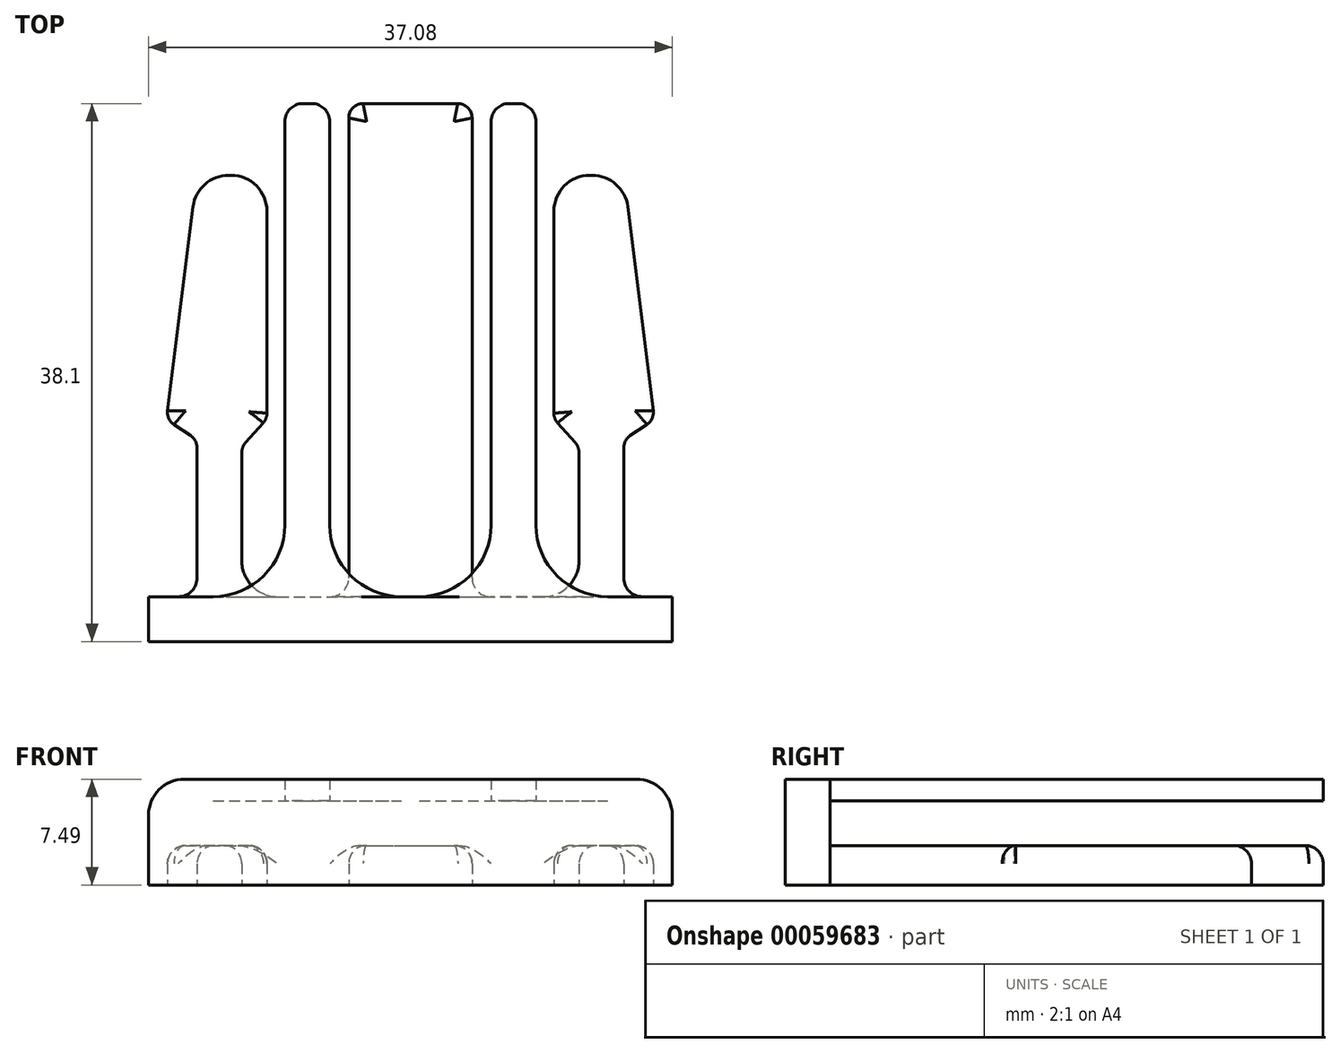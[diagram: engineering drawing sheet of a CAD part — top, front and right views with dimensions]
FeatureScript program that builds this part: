
annotation { "Feature Type Name" : "Feature", "Feature Type Description" : "" }
export const myFeature = defineFeature(function(context is Context, id is Id, definition is map)
    precondition{}
    {
        {
            var Q0;
            Q0=qCreatedBy(makeId("Top.planeOp"),FACE);
            var sketch = newSketch(context, id + "F0", { "sketchPlane" : qUnion([Q0])});
            skLineSegment(sketch, "E0", {"start": v(0, -24.5) * mm, "end": v(-18.54, -24.5) * mm});
            skLineSegment(sketch, "E1", {"start": v(-18.54, -24.5) * mm, "end": v(-18.54, -21.32) * mm});
            skLineSegment(sketch, "E2", {"start": v(-18.54, -21.32) * mm, "end": v(-15.11, -21.32) * mm});
            skLineSegment(sketch, "E3", {"start": v(-15.11, -21.32) * mm, "end": v(-15.11, -10.2) * mm});
            skLineSegment(sketch, "E4", {"start": v(-15.11, 8.53) * mm, "end": v(-11.94, 8.53) * mm});
            skLineSegment(sketch, "E5", {"start": v(-11.94, -10.7) * mm, "end": v(-11.94, -21.32) * mm});
            skLineSegment(sketch, "E6", {"start": v(-4.37, -21.32) * mm, "end": v(-4.37, 13.6) * mm});
            skLineSegment(sketch, "E7", {"start": v(-4.37, 13.6) * mm, "end": v(0, 13.6) * mm});
            skLineSegment(sketch, "E8", {"start": v(-15.11, -10.2) * mm, "end": v(-17.27, -8.78) * mm});
            skLineSegment(sketch, "E9", {"start": v(-17.27, -8.78) * mm, "end": v(-15.11, 8.53) * mm});
            skLineSegment(sketch, "E10", {"start": v(-11.94, 8.53) * mm, "end": v(-10.16, 8.53) * mm});
            skLineSegment(sketch, "E11", {"start": v(-10.16, 8.53) * mm, "end": v(-10.16, -8.7) * mm});
            skLineSegment(sketch, "E12", {"start": v(-10.16, -8.7) * mm, "end": v(-11.94, -10.7) * mm});
            skLineSegment(sketch, "E13.trimOffspring", {"start": v(-11.94, -21.32) * mm, "end": v(-4.37, -21.32) * mm});
            skLineSegment(sketch, "E14", {"start": v(0, 13.6) * mm, "end": v(0, 0) * mm});
            skLineSegment(sketch, "E15.MirrorCS", {"start": v(4.37, 13.6) * mm, "end": v(0, 13.6) * mm});
            skLineSegment(sketch, "E16.MirrorCS", {"start": v(4.37, -21.32) * mm, "end": v(4.37, 13.6) * mm});
            skLineSegment(sketch, "E17.MirrorCS", {"start": v(11.94, -21.32) * mm, "end": v(4.37, -21.32) * mm});
            skLineSegment(sketch, "E18.MirrorCS", {"start": v(11.94, -10.7) * mm, "end": v(11.94, -21.32) * mm});
            skLineSegment(sketch, "E19.MirrorCS", {"start": v(10.16, -8.7) * mm, "end": v(11.94, -10.7) * mm});
            skLineSegment(sketch, "E20.MirrorCS", {"start": v(10.16, 8.53) * mm, "end": v(10.16, -8.7) * mm});
            skLineSegment(sketch, "E21.MirrorCS", {"start": v(11.94, 8.53) * mm, "end": v(10.16, 8.53) * mm});
            skLineSegment(sketch, "E22.MirrorCS", {"start": v(15.11, 8.53) * mm, "end": v(11.94, 8.53) * mm});
            skLineSegment(sketch, "E23.MirrorCS", {"start": v(17.27, -8.78) * mm, "end": v(15.11, 8.53) * mm});
            skLineSegment(sketch, "E24.MirrorCS", {"start": v(15.11, -10.2) * mm, "end": v(17.27, -8.78) * mm});
            skLineSegment(sketch, "E25.MirrorCS", {"start": v(15.11, -21.32) * mm, "end": v(15.11, -10.2) * mm});
            skLineSegment(sketch, "E26.MirrorCS", {"start": v(18.54, -21.32) * mm, "end": v(15.11, -21.32) * mm});
            skLineSegment(sketch, "E27.MirrorCS", {"start": v(18.54, -24.5) * mm, "end": v(18.54, -21.32) * mm});
            skLineSegment(sketch, "E28.MirrorCS", {"start": v(0, -24.5) * mm, "end": v(18.54, -24.5) * mm});
            skSolve(sketch);
        }
        {
            var Q0;
            Q0=makeQuery(id+"F0.imprint","IMPRINT",FACE,{"disambiguationData":[TD([[makeQuery(id+"F0.imprint","IMPRINT",EDGE,{"derivedFrom":sQuery(id+"F0.wireOp",EDGE,"E0")}),-1.0]])]});
            extrude(context, id + "F1", {"entities" : qUnion([Q0]), "depth" : 2.8 * mm});
        }
        {
            var Q0;
            Q0=makeQuery(id+"F1.opExtrude","SWEPT_EDGE",EDGE,{"disambiguationData":[OSD([sQuery(id+"F0.wireOp",EDGE,"E8"),sQuery(id+"F0.wireOp",EDGE,"E9")])]});
            var Q1;
            Q1=makeQuery(id+"F1.opExtrude","SWEPT_EDGE",EDGE,{"disambiguationData":[OSD([sQuery(id+"F0.wireOp",EDGE,"E5"),sQuery(id+"F0.wireOp",EDGE,"E12")])]});
            var Q2;
            Q2=makeQuery(id+"F1.opExtrude","SWEPT_EDGE",EDGE,{"disambiguationData":[OSD([sQuery(id+"F0.wireOp",EDGE,"E11"),sQuery(id+"F0.wireOp",EDGE,"E12")])]});
            var Q3;
            Q3=makeQuery(id+"F1.opExtrude","SWEPT_EDGE",EDGE,{"disambiguationData":[OSD([sQuery(id+"F0.wireOp",EDGE,"5dbca827-9765-4d0b-b738-52eea5b91d420.MirrorCS"),sQuery(id+"F0.wireOp",EDGE,"41e8d5a4-3eae-4dab-9418-c4afa11fb4a70.MirrorCS")])]});
            var Q4;
            Q4=makeQuery(id+"F1.opExtrude","SWEPT_EDGE",EDGE,{"disambiguationData":[OSD([sQuery(id+"F0.wireOp",EDGE,"c12c2d76-7289-4d38-adec-d10e20b737c40.MirrorCS"),sQuery(id+"F0.wireOp",EDGE,"84a0010f-25cf-47dd-b195-3eac934034af0.MirrorCS")])]});
            var Q5;
            Q5=makeQuery(id+"F1.opExtrude","SWEPT_EDGE",EDGE,{"disambiguationData":[OSD([sQuery(id+"F0.wireOp",EDGE,"67a6e3c0-60ff-418f-9d16-aaa68642b8130.MirrorCS"),sQuery(id+"F0.wireOp",EDGE,"c12c2d76-7289-4d38-adec-d10e20b737c40.MirrorCS")])]});
            var Q6;
            Q6=makeQuery(id+"F1.opExtrude","SWEPT_EDGE",EDGE,{"disambiguationData":[OSD([sQuery(id+"F0.wireOp",EDGE,"E3"),sQuery(id+"F0.wireOp",EDGE,"E8")])]});
            var Q7;
            Q7=makeQuery(id+"F1.opExtrude","SWEPT_EDGE",EDGE,{"disambiguationData":[OSD([sQuery(id+"F0.wireOp",EDGE,"182dc025-4c15-4511-8ecc-ef8c38a5272f0.MirrorCS"),sQuery(id+"F0.wireOp",EDGE,"41e8d5a4-3eae-4dab-9418-c4afa11fb4a70.MirrorCS")])]});
            var Q8;
            Q8=makeQuery(id+"F1.opExtrude","SWEPT_EDGE",EDGE,{"disambiguationData":[OSD([sQuery(id+"F0.wireOp",EDGE,"f6ebb351-b71a-4f62-886c-60468f4f10860.MirrorCS"),sQuery(id+"F0.wireOp",EDGE,"eb93e29c-52ff-4c8f-8371-2f97ac019cd80.MirrorCS")])]});
            var Q9;
            Q9=makeQuery(id+"F1.opExtrude","SWEPT_EDGE",EDGE,{"disambiguationData":[OSD([sQuery(id+"F0.wireOp",EDGE,"E6"),sQuery(id+"F0.wireOp",EDGE,"E7")])]});
            var Q10;
            Q10=makeQuery(id+"F1.opExtrude","SWEPT_EDGE",EDGE,{"disambiguationData":[OSD([sQuery(id+"F0.wireOp",EDGE,"E15.MirrorCS"),sQuery(id+"F0.wireOp",EDGE,"E16.MirrorCS")])]});
            var Q11;
            Q11=makeQuery(id+"F1.opExtrude","SWEPT_EDGE",EDGE,{"disambiguationData":[OSD([sQuery(id+"F0.wireOp",EDGE,"E23.MirrorCS"),sQuery(id+"F0.wireOp",EDGE,"E24.MirrorCS")])]});
            var Q12;
            Q12=makeQuery(id+"F1.opExtrude","SWEPT_EDGE",EDGE,{"disambiguationData":[OSD([sQuery(id+"F0.wireOp",EDGE,"E24.MirrorCS"),sQuery(id+"F0.wireOp",EDGE,"E25.MirrorCS")])]});
            var Q13;
            Q13=makeQuery(id+"F1.opExtrude","SWEPT_EDGE",EDGE,{"disambiguationData":[OSD([sQuery(id+"F0.wireOp",EDGE,"E18.MirrorCS"),sQuery(id+"F0.wireOp",EDGE,"E19.MirrorCS")])]});
            var Q14;
            Q14=makeQuery(id+"F1.opExtrude","SWEPT_EDGE",EDGE,{"disambiguationData":[OSD([sQuery(id+"F0.wireOp",EDGE,"E19.MirrorCS"),sQuery(id+"F0.wireOp",EDGE,"E20.MirrorCS")])]});
            fillet(context, id + "F2", {"entities" : qUnion([Q0, Q1, Q2, Q3, Q4, Q5, Q6, Q7, Q8, Q9, Q10, Q11, Q12, Q13, Q14]), "radius" : 1.02 * mm, "tangentPropagation" : true, "allowEdgeOverflow" : false});
        }
        {
            var Q0;
            Q0=makeQuery(id+"F1.opExtrude","SWEPT_EDGE",EDGE,{"disambiguationData":[OSD([sQuery(id+"F0.wireOp",EDGE,"E2"),sQuery(id+"F0.wireOp",EDGE,"E3")])]});
            var Q1;
            Q1=makeQuery(id+"F1.opExtrude","SWEPT_EDGE",EDGE,{"disambiguationData":[OSD([sQuery(id+"F0.wireOp",EDGE,"043e1b75-f5ca-422c-ab0a-28e3224b58670.MirrorCS"),sQuery(id+"F0.wireOp",EDGE,"182dc025-4c15-4511-8ecc-ef8c38a5272f0.MirrorCS")])]});
            var Q2;
            Q2=makeQuery(id+"F1.opExtrude","SWEPT_EDGE",EDGE,{"disambiguationData":[OSD([sQuery(id+"F0.wireOp",EDGE,"eb93e29c-52ff-4c8f-8371-2f97ac019cd80.MirrorCS"),sQuery(id+"F0.wireOp",EDGE,"24293765-a530-4c86-9293-c4c4a651b3b3.trimOffspring")])]});
            var Q3;
            Q3=makeQuery(id+"F1.opExtrude","SWEPT_EDGE",EDGE,{"disambiguationData":[OSD([sQuery(id+"F0.wireOp",EDGE,"E6"),sQuery(id+"F0.wireOp",EDGE,"E13.trimOffspring")])]});
            var Q4;
            Q4=makeQuery(id+"F1.opExtrude","SWEPT_EDGE",EDGE,{"disambiguationData":[OSD([sQuery(id+"F0.wireOp",EDGE,"E16.MirrorCS"),sQuery(id+"F0.wireOp",EDGE,"E17.MirrorCS")])]});
            var Q5;
            Q5=makeQuery(id+"F1.opExtrude","SWEPT_EDGE",EDGE,{"disambiguationData":[OSD([sQuery(id+"F0.wireOp",EDGE,"E25.MirrorCS"),sQuery(id+"F0.wireOp",EDGE,"E26.MirrorCS")])]});
            fillet(context, id + "F3", {"entities" : qUnion([Q0, Q1, Q2, Q3, Q4, Q5]), "radius" : 1.32 * mm, "tangentPropagation" : true, "allowEdgeOverflow" : false});
        }
        {
            var Q0;
            Q0=makeQuery(id+"F1.opExtrude","SWEPT_EDGE",EDGE,{"disambiguationData":[OSD([sQuery(id+"F0.wireOp",EDGE,"67a6e3c0-60ff-418f-9d16-aaa68642b8130.MirrorCS"),sQuery(id+"F0.wireOp",EDGE,"24293765-a530-4c86-9293-c4c4a651b3b3.trimOffspring")])]});
            var Q1;
            Q1=makeQuery(id+"F1.opExtrude","SWEPT_EDGE",EDGE,{"disambiguationData":[OSD([sQuery(id+"F0.wireOp",EDGE,"E5"),sQuery(id+"F0.wireOp",EDGE,"E13.trimOffspring")])]});
            var Q2;
            Q2=makeQuery(id+"F1.opExtrude","SWEPT_EDGE",EDGE,{"disambiguationData":[OSD([sQuery(id+"F0.wireOp",EDGE,"44883f8e-5c6c-496e-87a4-7bb2ec8b31cd0.MirrorCS"),sQuery(id+"F0.wireOp",EDGE,"5dbca827-9765-4d0b-b738-52eea5b91d420.MirrorCS")])]});
            var Q3;
            Q3=makeQuery(id+"F1.opExtrude","SWEPT_EDGE",EDGE,{"disambiguationData":[OSD([sQuery(id+"F0.wireOp",EDGE,"84a0010f-25cf-47dd-b195-3eac934034af0.MirrorCS"),sQuery(id+"F0.wireOp",EDGE,"d00008af-d735-409f-bce0-33d418154a760.MirrorCS")])]});
            var Q4;
            Q4=makeQuery(id+"F1.opExtrude","SWEPT_EDGE",EDGE,{"disambiguationData":[OSD([sQuery(id+"F0.wireOp",EDGE,"E10"),sQuery(id+"F0.wireOp",EDGE,"E11")])]});
            var Q5;
            Q5=makeQuery(id+"F1.opExtrude","SWEPT_EDGE",EDGE,{"disambiguationData":[OSD([sQuery(id+"F0.wireOp",EDGE,"E4"),sQuery(id+"F0.wireOp",EDGE,"E9")])]});
            var Q6;
            Q6=makeQuery(id+"F1.opExtrude","SWEPT_EDGE",EDGE,{"disambiguationData":[OSD([sQuery(id+"F0.wireOp",EDGE,"E17.MirrorCS"),sQuery(id+"F0.wireOp",EDGE,"E18.MirrorCS")])]});
            var Q7;
            Q7=makeQuery(id+"F1.opExtrude","SWEPT_EDGE",EDGE,{"disambiguationData":[OSD([sQuery(id+"F0.wireOp",EDGE,"E20.MirrorCS"),sQuery(id+"F0.wireOp",EDGE,"E21.MirrorCS")])]});
            var Q8;
            Q8=makeQuery(id+"F1.opExtrude","SWEPT_EDGE",EDGE,{"disambiguationData":[OSD([sQuery(id+"F0.wireOp",EDGE,"E22.MirrorCS"),sQuery(id+"F0.wireOp",EDGE,"E23.MirrorCS")])]});
            fillet(context, id + "F4", {"entities" : qUnion([Q0, Q1, Q2, Q3, Q4, Q5, Q6, Q7, Q8]), "radius" : 2.54 * mm, "tangentPropagation" : true, "allowEdgeOverflow" : false});
        }
        {
            var Q0;
            Q0=makeQuery(id+"F1.opExtrude","CAP_FACE",FACE,{"disambiguationData":[OSD([sQuery(id+"F0.wireOp",EDGE,"E0"),sQuery(id+"F0.wireOp",EDGE,"E1"),sQuery(id+"F0.wireOp",EDGE,"E2"),sQuery(id+"F0.wireOp",EDGE,"E3"),sQuery(id+"F0.wireOp",EDGE,"E4"),sQuery(id+"F0.wireOp",EDGE,"E5"),sQuery(id+"F0.wireOp",EDGE,"E6"),sQuery(id+"F0.wireOp",EDGE,"E7"),sQuery(id+"F0.wireOp",EDGE,"E8"),sQuery(id+"F0.wireOp",EDGE,"E9"),sQuery(id+"F0.wireOp",EDGE,"E10"),sQuery(id+"F0.wireOp",EDGE,"E11"),sQuery(id+"F0.wireOp",EDGE,"E12"),sQuery(id+"F0.wireOp",EDGE,"E13.trimOffspring"),sQuery(id+"F0.wireOp",EDGE,"E15.MirrorCS"),sQuery(id+"F0.wireOp",EDGE,"E16.MirrorCS"),sQuery(id+"F0.wireOp",EDGE,"E17.MirrorCS"),sQuery(id+"F0.wireOp",EDGE,"E18.MirrorCS"),sQuery(id+"F0.wireOp",EDGE,"E19.MirrorCS"),sQuery(id+"F0.wireOp",EDGE,"E20.MirrorCS"),sQuery(id+"F0.wireOp",EDGE,"E21.MirrorCS"),sQuery(id+"F0.wireOp",EDGE,"E22.MirrorCS"),sQuery(id+"F0.wireOp",EDGE,"E23.MirrorCS"),sQuery(id+"F0.wireOp",EDGE,"E24.MirrorCS"),sQuery(id+"F0.wireOp",EDGE,"E25.MirrorCS"),sQuery(id+"F0.wireOp",EDGE,"E26.MirrorCS"),sQuery(id+"F0.wireOp",EDGE,"E27.MirrorCS"),sQuery(id+"F0.wireOp",EDGE,"E28.MirrorCS")])],"isStart":false});
            var sketch = newSketch(context, id + "F5", { "sketchPlane" : qUnion([Q0])});
            skLineSegment(sketch, "E29.bottom", {"start": v(-18.54, -24.5) * mm, "end": v(18.54, -24.5) * mm});
            skLineSegment(sketch, "E29.top", {"start": v(-18.54, -21.32) * mm, "end": v(18.54, -21.32) * mm});
            skLineSegment(sketch, "E29.left", {"start": v(-18.54, -24.5) * mm, "end": v(-18.54, -21.32) * mm});
            skLineSegment(sketch, "E29.right", {"start": v(18.54, -24.5) * mm, "end": v(18.54, -21.32) * mm});
            skSolve(sketch);
        }
        {
            var Q0;
            Q0 = qSketchRegion(id + "F5", true);
            extrude(context, id + "F6", {"entities" : qUnion([Q0]), "operationType" : NewBodyOperationType.ADD, "depth" : 3.17 * mm});
        }
        {
            var Q0;
            Q0=makeQuery(id+"F6.opExtrude","CAP_FACE",FACE,{"disambiguationData":[OSD([sQuery(id+"F5.wireOp",EDGE,"E29.bottom"),sQuery(id+"F5.wireOp",EDGE,"E29.top"),sQuery(id+"F5.wireOp",EDGE,"E29.left"),sQuery(id+"F5.wireOp",EDGE,"E29.right")])],"isStart":false});
            var sketch = newSketch(context, id + "F7", { "sketchPlane" : qUnion([Q0])});
            skLineSegment(sketch, "E30.bottom", {"start": v(-8.89, -24.5) * mm, "end": v(-5.71, -24.5) * mm});
            skLineSegment(sketch, "E30.top", {"start": v(-8.9, 13.6) * mm, "end": v(-5.72, 13.6) * mm});
            skLineSegment(sketch, "E30.left", {"start": v(-8.89, -21.32) * mm, "end": v(-8.9, 13.6) * mm});
            skLineSegment(sketch, "E30.right", {"start": v(-5.71, -21.32) * mm, "end": v(-5.72, 13.6) * mm});
            skLineSegment(sketch, "E31.MirrorCS", {"start": v(5.71, -21.32) * mm, "end": v(5.72, 13.6) * mm});
            skLineSegment(sketch, "E32.MirrorCS", {"start": v(8.9, 13.6) * mm, "end": v(5.72, 13.6) * mm});
            skLineSegment(sketch, "E33.MirrorCS", {"start": v(8.89, -21.32) * mm, "end": v(8.9, 13.6) * mm});
            skLineSegment(sketch, "E34.MirrorCS", {"start": v(8.89, -24.5) * mm, "end": v(5.71, -24.5) * mm});
            skLineSegment(sketch, "E35.bottom", {"start": v(-18.54, -24.5) * mm, "end": v(18.54, -24.5) * mm});
            skLineSegment(sketch, "E35.top", {"start": v(-18.54, -21.32) * mm, "end": v(-8.89, -21.32) * mm});
            skLineSegment(sketch, "E35.left", {"start": v(-18.54, -24.5) * mm, "end": v(-18.54, -21.32) * mm});
            skLineSegment(sketch, "E35.right", {"start": v(18.54, -24.5) * mm, "end": v(18.54, -21.32) * mm});
            skLineSegment(sketch, "E36.trimOffspring", {"start": v(-5.71, -21.32) * mm, "end": v(5.71, -21.32) * mm});
            skPoint(sketch, "E37.orphan", {"position": v(5.71, -24.5) * mm});
            skLineSegment(sketch, "E38.trimOffspring", {"start": v(8.89, -21.32) * mm, "end": v(18.54, -21.32) * mm});
            skPoint(sketch, "E39.orphan", {"position": v(8.89, -24.5) * mm});
            skSolve(sketch);
        }
        {
            var Q0;
            Q0 = qSketchRegion(id + "F7", true);
            extrude(context, id + "F8", {"entities" : qUnion([Q0]), "operationType" : NewBodyOperationType.ADD, "depth" : 1.52 * mm});
        }
        {
            var Q0;
            Q0=makeQuery(id+"F8.opExtrude","SWEPT_EDGE",EDGE,{"disambiguationData":[OSD([sQuery(id+"F5.wireOp",EDGE,"E29.top"),sQuery(id+"F7.wireOp",EDGE,"E33.MirrorCS"),sQuery(id+"F7.wireOp",EDGE,"E38.trimOffspring")])]});
            var Q1;
            Q1=makeQuery(id+"F8.opExtrude","SWEPT_EDGE",EDGE,{"disambiguationData":[OSD([sQuery(id+"F5.wireOp",EDGE,"E29.top"),sQuery(id+"F7.wireOp",EDGE,"E31.MirrorCS"),sQuery(id+"F7.wireOp",EDGE,"E36.trimOffspring")])]});
            var Q2;
            Q2=makeQuery(id+"F8.opExtrude","SWEPT_EDGE",EDGE,{"disambiguationData":[OSD([sQuery(id+"F5.wireOp",EDGE,"E29.top"),sQuery(id+"F7.wireOp",EDGE,"E30.right"),sQuery(id+"F7.wireOp",EDGE,"E36.trimOffspring")])]});
            var Q3;
            Q3=makeQuery(id+"F8.opExtrude","SWEPT_EDGE",EDGE,{"disambiguationData":[OSD([sQuery(id+"F5.wireOp",EDGE,"E29.top"),sQuery(id+"F7.wireOp",EDGE,"E30.left"),sQuery(id+"F7.wireOp",EDGE,"E35.top")])]});
            fillet(context, id + "F9", {"entities" : qUnion([Q0, Q1, Q2, Q3]), "radius" : 5.08 * mm, "tangentPropagation" : true, "allowEdgeOverflow" : false});
        }
        {
            var Q0;
            Q0=makeQuery(id+"F1.opExtrude","CAP_EDGE",EDGE,{"disambiguationData":[OSD([sQuery(id+"F0.wireOp",EDGE,"E9")])],"isStart":false});
            var Q1;
            {var subQ0=sQuery(id+"F0.wireOp",EDGE,"E9");var subQ1=sQuery(id+"F0.wireOp",EDGE,"E4");Q1=makeQuery(id+"F4.opFillet","BLEND_EDGE",EDGE,{"blendedFrom":[makeQuery(id+"F1.opExtrude","SWEPT_EDGE",EDGE,{"disambiguationData":[OSD([subQ1,subQ0])]}),makeQuery(id+"F1.opExtrude","CAP_FACE",FACE,{"disambiguationData":[OSD([sQuery(id+"F0.wireOp",EDGE,"E0"),sQuery(id+"F0.wireOp",EDGE,"E1"),sQuery(id+"F0.wireOp",EDGE,"E2"),sQuery(id+"F0.wireOp",EDGE,"E3"),subQ1,sQuery(id+"F0.wireOp",EDGE,"E5"),sQuery(id+"F0.wireOp",EDGE,"E6"),sQuery(id+"F0.wireOp",EDGE,"E7"),sQuery(id+"F0.wireOp",EDGE,"E8"),subQ0,sQuery(id+"F0.wireOp",EDGE,"E10"),sQuery(id+"F0.wireOp",EDGE,"E11"),sQuery(id+"F0.wireOp",EDGE,"E12"),sQuery(id+"F0.wireOp",EDGE,"E13.trimOffspring"),sQuery(id+"F0.wireOp",EDGE,"E15.MirrorCS"),sQuery(id+"F0.wireOp",EDGE,"E16.MirrorCS"),sQuery(id+"F0.wireOp",EDGE,"E17.MirrorCS"),sQuery(id+"F0.wireOp",EDGE,"E18.MirrorCS"),sQuery(id+"F0.wireOp",EDGE,"E19.MirrorCS"),sQuery(id+"F0.wireOp",EDGE,"E20.MirrorCS"),sQuery(id+"F0.wireOp",EDGE,"E21.MirrorCS"),sQuery(id+"F0.wireOp",EDGE,"E22.MirrorCS"),sQuery(id+"F0.wireOp",EDGE,"E23.MirrorCS"),sQuery(id+"F0.wireOp",EDGE,"E24.MirrorCS"),sQuery(id+"F0.wireOp",EDGE,"E25.MirrorCS"),sQuery(id+"F0.wireOp",EDGE,"E26.MirrorCS"),sQuery(id+"F0.wireOp",EDGE,"E27.MirrorCS"),sQuery(id+"F0.wireOp",EDGE,"E28.MirrorCS")])],"isStart":false})],"blendedInto":[makeQuery(id+"F1.opExtrude","CAP_FACE",FACE,{"disambiguationData":[OSD([sQuery(id+"F0.wireOp",EDGE,"E0"),sQuery(id+"F0.wireOp",EDGE,"E1"),sQuery(id+"F0.wireOp",EDGE,"E2"),sQuery(id+"F0.wireOp",EDGE,"E3"),subQ1,sQuery(id+"F0.wireOp",EDGE,"E5"),sQuery(id+"F0.wireOp",EDGE,"E6"),sQuery(id+"F0.wireOp",EDGE,"E7"),sQuery(id+"F0.wireOp",EDGE,"E8"),subQ0,sQuery(id+"F0.wireOp",EDGE,"E10"),sQuery(id+"F0.wireOp",EDGE,"E11"),sQuery(id+"F0.wireOp",EDGE,"E12"),sQuery(id+"F0.wireOp",EDGE,"E13.trimOffspring"),sQuery(id+"F0.wireOp",EDGE,"E15.MirrorCS"),sQuery(id+"F0.wireOp",EDGE,"E16.MirrorCS"),sQuery(id+"F0.wireOp",EDGE,"E17.MirrorCS"),sQuery(id+"F0.wireOp",EDGE,"E18.MirrorCS"),sQuery(id+"F0.wireOp",EDGE,"E19.MirrorCS"),sQuery(id+"F0.wireOp",EDGE,"E20.MirrorCS"),sQuery(id+"F0.wireOp",EDGE,"E21.MirrorCS"),sQuery(id+"F0.wireOp",EDGE,"E22.MirrorCS"),sQuery(id+"F0.wireOp",EDGE,"E23.MirrorCS"),sQuery(id+"F0.wireOp",EDGE,"E24.MirrorCS"),sQuery(id+"F0.wireOp",EDGE,"E25.MirrorCS"),sQuery(id+"F0.wireOp",EDGE,"E26.MirrorCS"),sQuery(id+"F0.wireOp",EDGE,"E27.MirrorCS"),sQuery(id+"F0.wireOp",EDGE,"E28.MirrorCS")])],"isStart":false})]});}
            var Q2;
            Q2=makeQuery(id+"F1.opExtrude","CAP_EDGE",EDGE,{"disambiguationData":[OSD([sQuery(id+"F0.wireOp",EDGE,"E8")])],"isStart":false});
            var Q3;
            Q3=makeQuery(id+"F1.opExtrude","CAP_EDGE",EDGE,{"disambiguationData":[OSD([sQuery(id+"F0.wireOp",EDGE,"E3")])],"isStart":false});
            var Q4;
            Q4=makeQuery(id+"F1.opExtrude","CAP_EDGE",EDGE,{"disambiguationData":[OSD([sQuery(id+"F0.wireOp",EDGE,"E23.MirrorCS")])],"isStart":false});
            var Q5;
            Q5=makeQuery(id+"F1.opExtrude","CAP_EDGE",EDGE,{"disambiguationData":[OSD([sQuery(id+"F0.wireOp",EDGE,"E6")])],"isStart":false});
            var Q6;
            Q6=makeQuery(id+"F8.opExtrude","SWEPT_EDGE",EDGE,{"disambiguationData":[OSD([sQuery(id+"F7.wireOp",EDGE,"E30.top"),sQuery(id+"F7.wireOp",EDGE,"E30.left")])]});
            var Q7;
            Q7=makeQuery(id+"F8.opExtrude","SWEPT_EDGE",EDGE,{"disambiguationData":[OSD([sQuery(id+"F7.wireOp",EDGE,"E30.top"),sQuery(id+"F7.wireOp",EDGE,"E30.right")])]});
            var Q8;
            Q8=makeQuery(id+"F8.opExtrude","SWEPT_EDGE",EDGE,{"disambiguationData":[OSD([sQuery(id+"F7.wireOp",EDGE,"E31.MirrorCS"),sQuery(id+"F7.wireOp",EDGE,"E32.MirrorCS")])]});
            var Q9;
            Q9=makeQuery(id+"F8.opExtrude","SWEPT_EDGE",EDGE,{"disambiguationData":[OSD([sQuery(id+"F7.wireOp",EDGE,"E32.MirrorCS"),sQuery(id+"F7.wireOp",EDGE,"E33.MirrorCS")])]});
            fillet(context, id + "F10", {"entities" : qUnion([Q0, Q1, Q2, Q3, Q4, Q5, Q6, Q7, Q8, Q9]), "radius" : 1.27 * mm, "tangentPropagation" : true, "allowEdgeOverflow" : false});
        }
        {
            var Q0;
            Q0=makeQuery(id+"F8.opExtrude","CAP_EDGE",EDGE,{"disambiguationData":[OSD([sQuery(id+"F7.wireOp",EDGE,"E35.left")])],"isStart":false});
            var Q1;
            Q1=makeQuery(id+"F8.opExtrude","CAP_EDGE",EDGE,{"disambiguationData":[OSD([sQuery(id+"F7.wireOp",EDGE,"E35.right")])],"isStart":false});
            fillet(context, id + "F11", {"entities" : qUnion([Q0, Q1]), "radius" : 2.54 * mm, "tangentPropagation" : true, "allowEdgeOverflow" : false});
        }
    });
